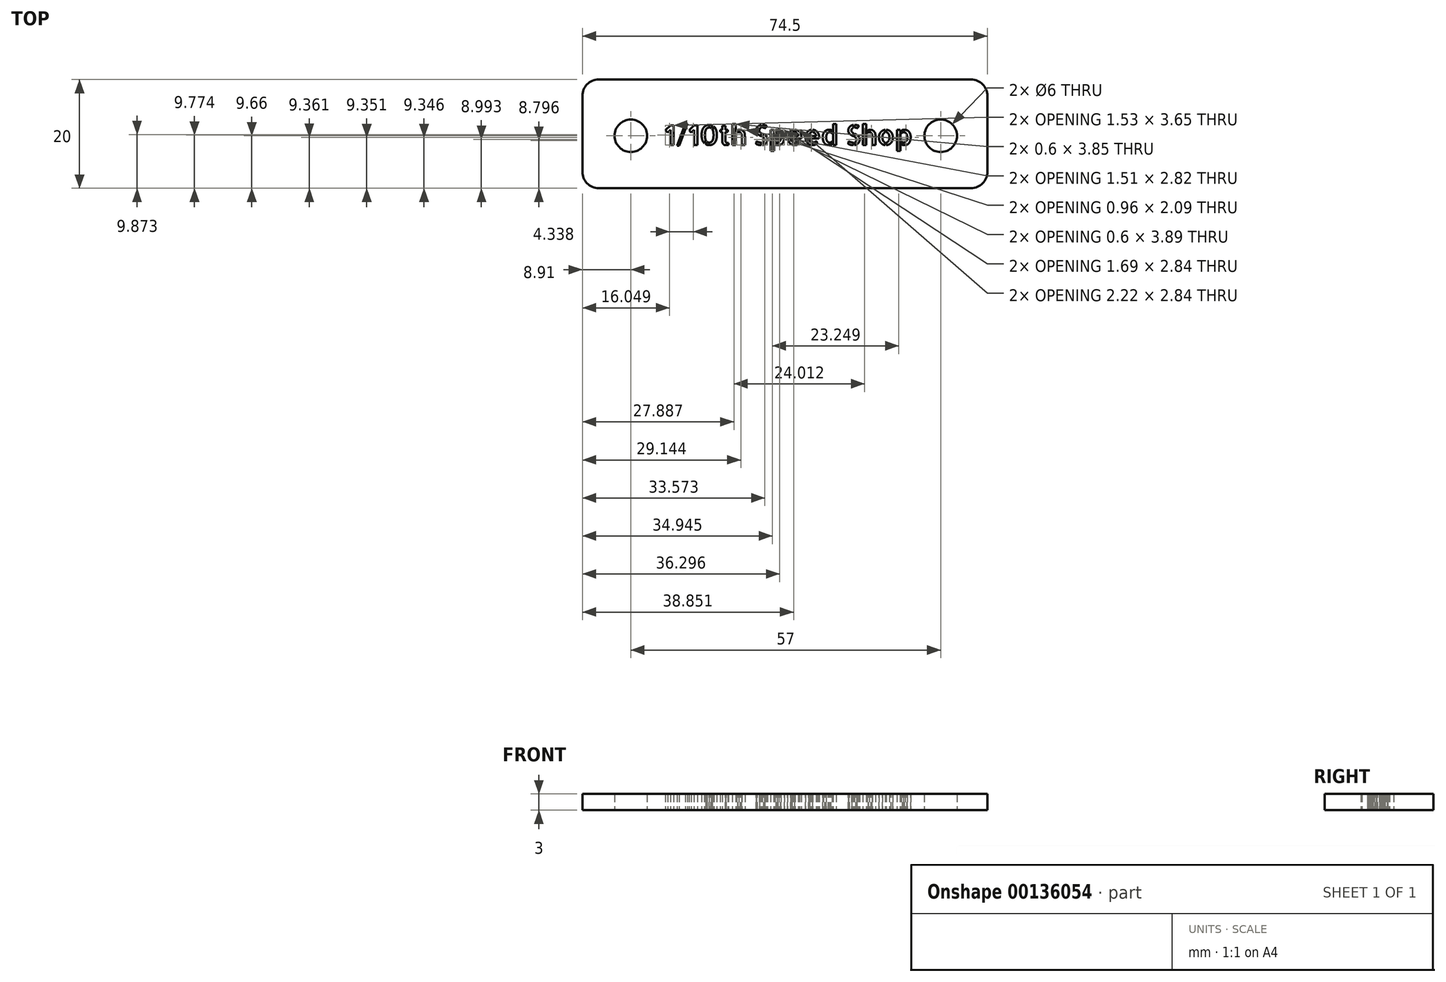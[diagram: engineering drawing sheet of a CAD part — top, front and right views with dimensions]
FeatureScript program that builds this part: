
annotation { "Feature Type Name" : "Feature", "Feature Type Description" : "" }
export const myFeature = defineFeature(function(context is Context, id is Id, definition is map)
    precondition{}
    {
        {
            var Q0;
            Q0=qCreatedBy(makeId("Top.planeOp"),FACE);
            var sketch = newSketch(context, id + "F0", { "sketchPlane" : qUnion([Q0])});
            skLineSegment(sketch, "E0.bottom", {"start": v(-33.24, 10.34) * mm, "end": v(35.26, 10.34) * mm});
            skLineSegment(sketch, "E0.top", {"start": v(-33.24, -9.66) * mm, "end": v(35.26, -9.66) * mm});
            skLineSegment(sketch, "E0.left", {"start": v(-36.24, 7.34) * mm, "end": v(-36.24, -6.66) * mm});
            skLineSegment(sketch, "E0.right", {"start": v(38.26, 7.34) * mm, "end": v(38.26, -6.66) * mm});
            skCircle(sketch, "E1", {"center": v(-27.33, 0) * mm, "radius": 3 * mm});
            skCircle(sketch, "E2", {"center": v(29.67, 0) * mm, "radius": 3 * mm});
            skPoint(sketch, "E3.visualSharp", {"position": v(-36.24, 10.34) * mm});
            skArc(sketch, "E3.filletArc", {"start": v(-33.24, 10.34) * mm, "mid": v(-35.36, 9.47) * mm, "end": v(-36.24, 7.34) * mm});
            skPoint(sketch, "E4.visualSharp", {"position": v(-36.24, -9.66) * mm});
            skArc(sketch, "E4.filletArc", {"start": v(-36.24, -6.66) * mm, "mid": v(-35.36, -8.78) * mm, "end": v(-33.24, -9.66) * mm});
            skPoint(sketch, "E5.visualSharp", {"position": v(38.26, -9.66) * mm});
            skArc(sketch, "E5.filletArc", {"start": v(35.26, -9.66) * mm, "mid": v(37.38, -8.78) * mm, "end": v(38.26, -6.66) * mm});
            skPoint(sketch, "E6.visualSharp", {"position": v(38.26, 10.34) * mm});
            skArc(sketch, "E6.filletArc", {"start": v(38.26, 7.34) * mm, "mid": v(37.38, 9.47) * mm, "end": v(35.26, 10.34) * mm});
            skText(sketch, "E7", { "text": "1/10th Speed Shop\n", "fontName": "AllertaStencil-Regular.ttf"});
            const initialGuessF0  = {"E7": [-0.0211, -0.00171, 1, 0, 0.00365]};
            skSetInitialGuess(sketch, initialGuessF0);
            skSolve(sketch);
        }
        {
            var Q0;
            Q0=makeQuery(id+"F0.imprint","IMPRINT",FACE,{"disambiguationData":[TD([[makeQuery(id+"F0.imprint","IMPRINT",EDGE,{"derivedFrom":sQuery(id+"F0.wireOp",EDGE,"E0.bottom")}),-1.0]])]});
            extrude(context, id + "F1", {"entities" : qUnion([Q0]), "depth" : 3 * mm});
        }
    });
